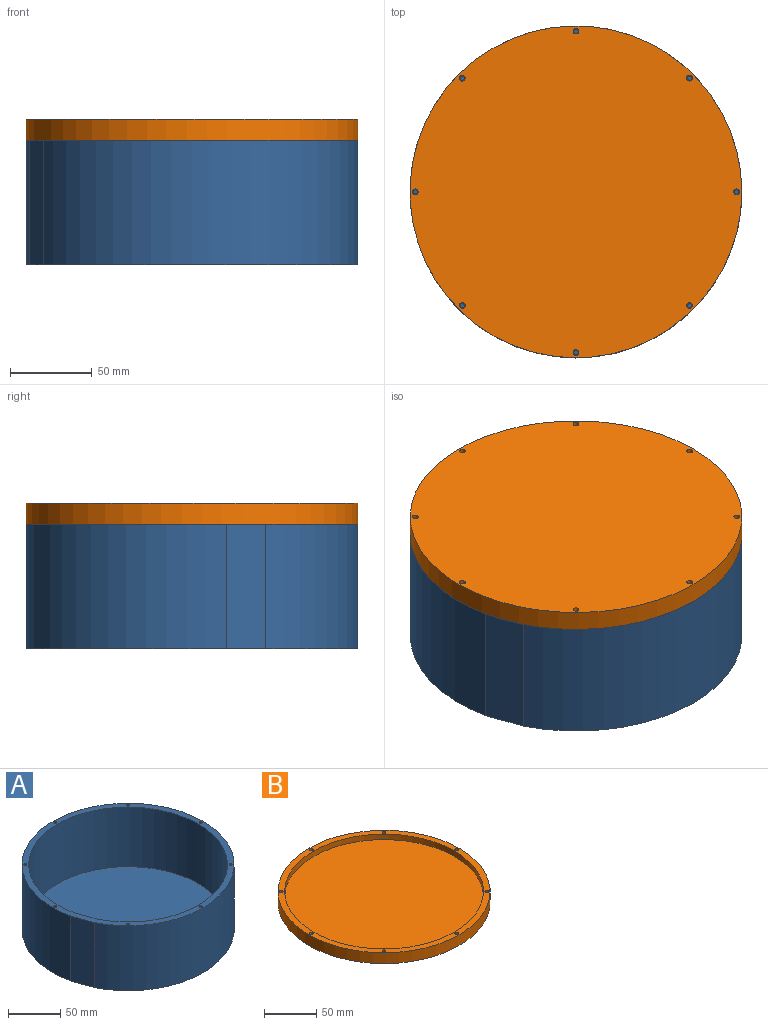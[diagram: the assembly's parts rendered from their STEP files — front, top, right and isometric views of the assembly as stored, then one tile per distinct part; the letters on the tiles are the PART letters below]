
ASSEMBLY  parts=2 mates=1
PART A: 23 faces, bbox 203.2x203.2x76.2 mm
  f0: plane 76.2x23.99mm, normal (-0.94,-0.33,0), area 1935.5mm2, adj f1,f2,f3
  f1: cylinder r=101.6mm len=203.2mm, axis (0,0,-1), area 46703.4mm2, adj f0,f2,f3
  f2: plane 203.2x203.2mm, normal (0,0,1), area 3881.5mm2, adj f0,f1,f4,f5,f7,f9,f11,f13
  f3: plane 203.2x203.2mm, normal (0,0,-1), area 32415.8mm2, adj f0,f1
  f4: plane 69.85x23.99mm, normal (0.94,0.33,0), area 1774.2mm2, adj f2,f5,f6
  f5: cylinder r=95.25mm len=190.5mm, axis (0,0,1), area 40023.9mm2, adj f2,f4,f6
  f6: plane 190.5x190.5mm, normal (0,0,1), area 28487.9mm2, adj f4,f5
  f7: cylinder r=1.36mm len=25.4mm, axis (0,0,1), area 216.9mm2, adj f2,f8
  f8: plane 2.72x2.72mm, normal (0,0,1), area 5.8mm2, adj f7
  f9: cylinder r=1.36mm len=25.4mm, axis (0,0,1), area 216.9mm2, adj f2,f10
  f10: plane 2.72x2.72mm, normal (0,0,1), area 5.8mm2, adj f9
  f11: cylinder r=1.36mm len=25.4mm, axis (0,0,1), area 216.9mm2, adj f2,f12
  f12: plane 2.72x2.72mm, normal (0,0,1), area 5.8mm2, adj f11
  f13: cylinder r=1.36mm len=25.4mm, axis (0,0,1), area 216.9mm2, adj f2,f14
  f14: plane 2.72x2.72mm, normal (0,0,1), area 5.8mm2, adj f13
  f15: cylinder r=1.36mm len=25.4mm, axis (0,0,1), area 216.9mm2, adj f2,f16
  f16: plane 2.72x2.72mm, normal (0,0,1), area 5.8mm2, adj f15
  f17: cylinder r=1.36mm len=25.4mm, axis (0,0,1), area 216.9mm2, adj f2,f18
  f18: plane 2.72x2.72mm, normal (0,0,1), area 5.8mm2, adj f17
  f19: cylinder r=1.36mm len=25.4mm, axis (0,0,1), area 216.9mm2, adj f2,f20
  f20: plane 2.72x2.72mm, normal (0,0,1), area 5.8mm2, adj f19
  f21: cylinder r=1.36mm len=25.4mm, axis (0,0,1), area 216.9mm2, adj f2,f22
  f22: plane 2.72x2.72mm, normal (0,0,1), area 5.8mm2, adj f21
PART B: 13 faces, bbox 203.2x203.2x12.7 mm
  f0: cylinder r=101.6mm len=203.2mm, axis (0,0,-1), area 8107.3mm2, adj f1,f2
  f1: plane 203.2x203.2mm, normal (0,0,1), area 3849.8mm2, adj f0,f3,f5,f6,f7,f8,f9,f10
  f2: plane 203.2x203.2mm, normal (0,0,-1), area 32352.1mm2, adj f0,f5,f6,f7,f8,f9,f10,f11
  f3: cylinder r=95.25mm len=190.5mm, axis (0,0,1), area 3800.3mm2, adj f1,f4
  f4: plane 190.5x190.5mm, normal (0,0,1), area 28502.3mm2, adj f3
  f5: cylinder r=1.75mm len=12.7mm, axis (0,0,1), area 139.9mm2, adj f1,f2
  f6: cylinder r=1.75mm len=12.7mm, axis (0,0,1), area 139.9mm2, adj f1,f2
  f7: cylinder r=1.75mm len=12.7mm, axis (0,0,1), area 139.9mm2, adj f1,f2
  f8: cylinder r=1.75mm len=12.7mm, axis (0,0,1), area 139.9mm2, adj f1,f2
  f9: cylinder r=1.75mm len=12.7mm, axis (0,0,1), area 139.9mm2, adj f1,f2
  f10: cylinder r=1.75mm len=12.7mm, axis (0,0,1), area 139.9mm2, adj f1,f2
  f11: cylinder r=1.75mm len=12.7mm, axis (0,0,1), area 139.9mm2, adj f1,f2
  f12: cylinder r=1.75mm len=12.7mm, axis (0,0,1), area 139.9mm2, adj f1,f2
PLACE A at identity fixed
PLACE B rot(axis=(1,0,0),180deg) t=(0,0,88.9)mm
MATE revolute B.f8 <-> A.f9  axis (0,0,-1) through (0,-98.42,76.2)mm
